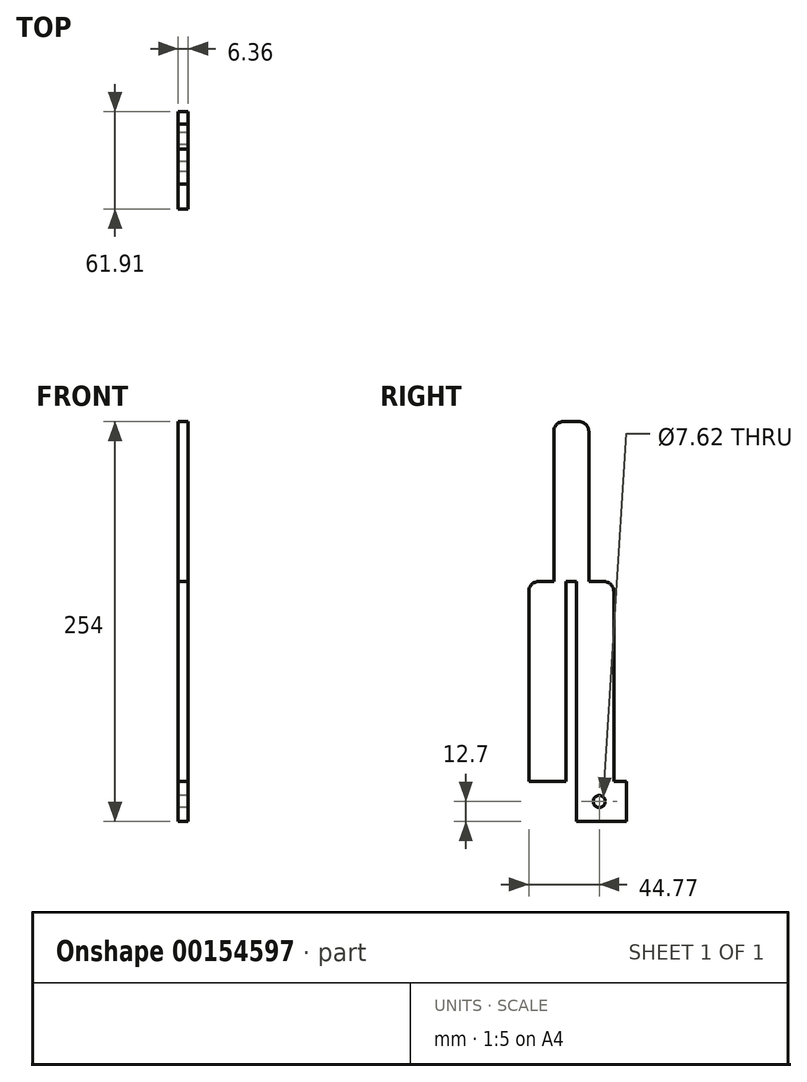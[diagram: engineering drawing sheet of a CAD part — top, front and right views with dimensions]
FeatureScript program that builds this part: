
annotation { "Feature Type Name" : "Feature", "Feature Type Description" : "" }
export const myFeature = defineFeature(function(context is Context, id is Id, definition is map)
    precondition{}
    {
        {
            var Q0;
            Q0=qCreatedBy(makeId("Right.planeOp"),FACE);
            var sketch = newSketch(context, id + "F0", { "sketchPlane" : qUnion([Q0])});
            skLineSegment(sketch, "E0.bottom", {"start": v(26.99, -63.5) * mm, "end": v(3.18, -63.5) * mm});
            skLineSegment(sketch, "E0.top", {"start": v(20.64, 63.5) * mm, "end": v(17.46, 63.5) * mm});
            skLineSegment(sketch, "E0.left", {"start": v(26.99, -63.5) * mm, "end": v(26.99, 57.15) * mm});
            skLineSegment(sketch, "E0.right", {"start": v(-26.99, -63.5) * mm, "end": v(-26.99, 57.15) * mm});
            skPoint(sketch, "E0.middle", {"position": v(0, 0) * mm});
            skLineSegment(sketch, "E1", {"start": v(-11.1, 63.5) * mm, "end": v(-11.1, 158.75) * mm});
            skLineSegment(sketch, "E2", {"start": v(-4.75, 165.1) * mm, "end": v(4.77, 165.1) * mm});
            skLineSegment(sketch, "E3", {"start": v(11.12, 158.75) * mm, "end": v(11.11, 63.5) * mm});
            skLineSegment(sketch, "E4.trimOffspring", {"start": v(-17.45, 63.5) * mm, "end": v(-20.64, 63.5) * mm});
            skPoint(sketch, "E5.start.orphan", {"position": v(0, -63.5) * mm});
            skPoint(sketch, "E6.visualSharp", {"position": v(-11.1, 63.5) * mm});
            skPoint(sketch, "E7.visualSharp", {"position": v(11.11, 63.5) * mm});
            skPoint(sketch, "E8.visualSharp", {"position": v(-26.99, 63.5) * mm});
            skArc(sketch, "E8.filletArc", {"start": v(-20.64, 63.5) * mm, "mid": v(-25.13, 61.64) * mm, "end": v(-26.99, 57.15) * mm});
            skPoint(sketch, "E9.visualSharp", {"position": v(26.99, 63.5) * mm});
            skArc(sketch, "E9.filletArc", {"start": v(26.99, 57.15) * mm, "mid": v(25.13, 61.64) * mm, "end": v(20.64, 63.5) * mm});
            skPoint(sketch, "E10.visualSharp", {"position": v(11.13, 165.1) * mm});
            skArc(sketch, "E10.filletArc", {"start": v(11.12, 158.75) * mm, "mid": v(9.26, 163.24) * mm, "end": v(4.77, 165.1) * mm});
            skPoint(sketch, "E11.visualSharp", {"position": v(-11.1, 165.1) * mm});
            skArc(sketch, "E11.filletArc", {"start": v(-4.75, 165.1) * mm, "mid": v(-9.24, 163.24) * mm, "end": v(-11.1, 158.75) * mm});
            skLineSegment(sketch, "E12", {"start": v(-3.18, -63.5) * mm, "end": v(-3.18, 63.5) * mm});
            skLineSegment(sketch, "E13", {"start": v(-3.18, 63.5) * mm, "end": v(3.17, 63.5) * mm});
            skLineSegment(sketch, "E14", {"start": v(3.17, 63.5) * mm, "end": v(3.17, -63.5) * mm});
            skLineSegment(sketch, "E15.trimOffspring", {"start": v(-3.18, -63.5) * mm, "end": v(-26.99, -63.5) * mm});
            skLineSegment(sketch, "E16.bottom", {"start": v(3.18, -63.5) * mm, "end": v(34.92, -63.5) * mm});
            skLineSegment(sketch, "E16.top", {"start": v(3.18, -88.9) * mm, "end": v(34.92, -88.9) * mm});
            skLineSegment(sketch, "E16.left", {"start": v(3.18, -63.5) * mm, "end": v(3.18, -88.9) * mm});
            skLineSegment(sketch, "E16.right", {"start": v(34.92, -63.5) * mm, "end": v(34.92, -88.9) * mm});
            skCircle(sketch, "E17", {"center": v(17.78, -76.2) * mm, "radius": 3.81 * mm});
            skPoint(sketch, "E17.centerSnap0", {"position": v(34.92, -76.2) * mm});
            skLineSegment(sketch, "E18", {"start": v(-17.45, 63.5) * mm, "end": v(-11.1, 63.5) * mm});
            skLineSegment(sketch, "E19", {"start": v(11.11, 63.5) * mm, "end": v(17.46, 63.5) * mm});
            skSolve(sketch);
        }
        {
            var Q0;
            Q0=qSketchRegion(id+"F0",true);
            extrude(context, id + "F1", {"entities" : qUnion([Q0]), "endBound" : BoundingType.SYMMETRIC, "depth" : 6.35 * mm});
        }
    });
